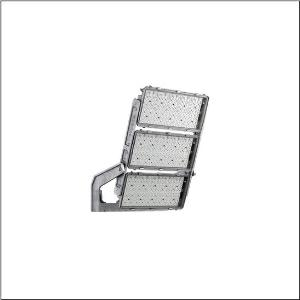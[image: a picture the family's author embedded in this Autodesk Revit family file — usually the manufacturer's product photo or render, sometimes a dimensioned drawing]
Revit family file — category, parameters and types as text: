
# Revit family: floodlight_fl_11_maxi_pro_remote___pl33tblc_5xa779425h01aa_685d
name_source: partatom
category: Lighting Fixtures
units: mm (PartAtom-declared; Revit-internal decimal feet)

## family parameters
Cut with Voids When Loaded = No
Host = Face
Light Source = No
Part Type = Normal
Room Calculation Point = No
Round Connector Dimension = Use Diameter
Shared = No

## types (1)
- --- (1 x LED, 117060 lm, 1335.4 W, 3000K)
    Apparent Load = 1335 VA
    CIE Flux Codes = 24 77 100 100 100
    Color Rendering = 70
    Color Temperature = 3000K
    Default Elevation = 1800 mm
    Description = Floodlight FL 11  maxi  pro Remote floodlight; light control with lens of PMMA; cover panel of toughened safety glass, transparent; light distribution: PL33TBLC, asymmetric direct distribution, LEDcolour temperature: 3000K, rated luminous flux: 117.060lm, colour rendering: CRI > 70, light colour: 730; luminous efficacy: 88lm/W; brightness control: DALI 2 (1 DALI address); with terminal, 8-pole, max. 2.5mm², mains connection: 220..240V/380..400V AC, 50/60Hz, surge voltage resistance: line to ground: 10kV, ECG replaceable separately, LED unit replaceable without ESD environment, dustproof LED module, dimming range 10..100%, no afterglow with DALI off / DMX off command; 1335W floodlight with 2x LED unit of diecast aluminium, coated grey; length: 713mm / width: 651mm / height: 338mm; mounting bracket, of diecast aluminium, uncoated, natural, equipment: Power, protection rating (complete): IP66; insulation class (complete): insulation class I (protective earthing); certification: CE, ENEC, VDE; ball protection: ball impact resistance with accessories, impact resistance: IK07; rated ambient temperature 10°C, only for outdoor installations, permissible operating ambient temperature: -40..+30°C, permissible storage temperature: -40..+85°C; packaging unit: 1 piece

Light Distribution: PL33TBLC
    Height = 320 mm
    Lamp = 1 x LED
    Lamp Light Flux = 117060 lm
    Lamp Power = 1335.4 W
    Lamp count = 1
    Length = 1002 mm
    Luminous efficacy = 88 lm/W
    Manufacturer = Siteco
    ModVariant = No
    Model = 5XA779425H01AA
    Mounting Place = Ceiling
    Mounting Type = Surface mounted
    Number of Poles = 1
    OnlyDefault = Yes
    Power Factor = 1
    Product Name = Floodlight FL 11 maxi pro Remote | PL33TBLC
    Product group = floodlight | ceiling mounted
    ProductGroupID = 302
    Protection Class = Protection class I
    Protection Degree = IP 66
    RLX_Detail_Level = 1
    RLX_Emergency_Light_Flux = 0 lm
    RLX_Emergency_Type = 0
    RLX_Emergency_Type_DB = No
    RlxData = <blob elided: 52077 chars, md5=49096b81>
    Socket = socket
    Standby Power = 0 W
    System Light Flux = 117060 lm
    System Power = 1335 W
    Type Comments = factory setting: luminous flux: 100 % | dim-lin: 254 | 920 mA
    Type Image = l_1006784.jpg
    URL = http://relux.com
    VarID = @adj_026511
    Voltage = 0 V
    Weight = 0.00 kg
    Width = 655 mm

## geometry (parser evidence)
native form markers: Blend x4, Sweep x13
no freeform markers — native parametric forms only
